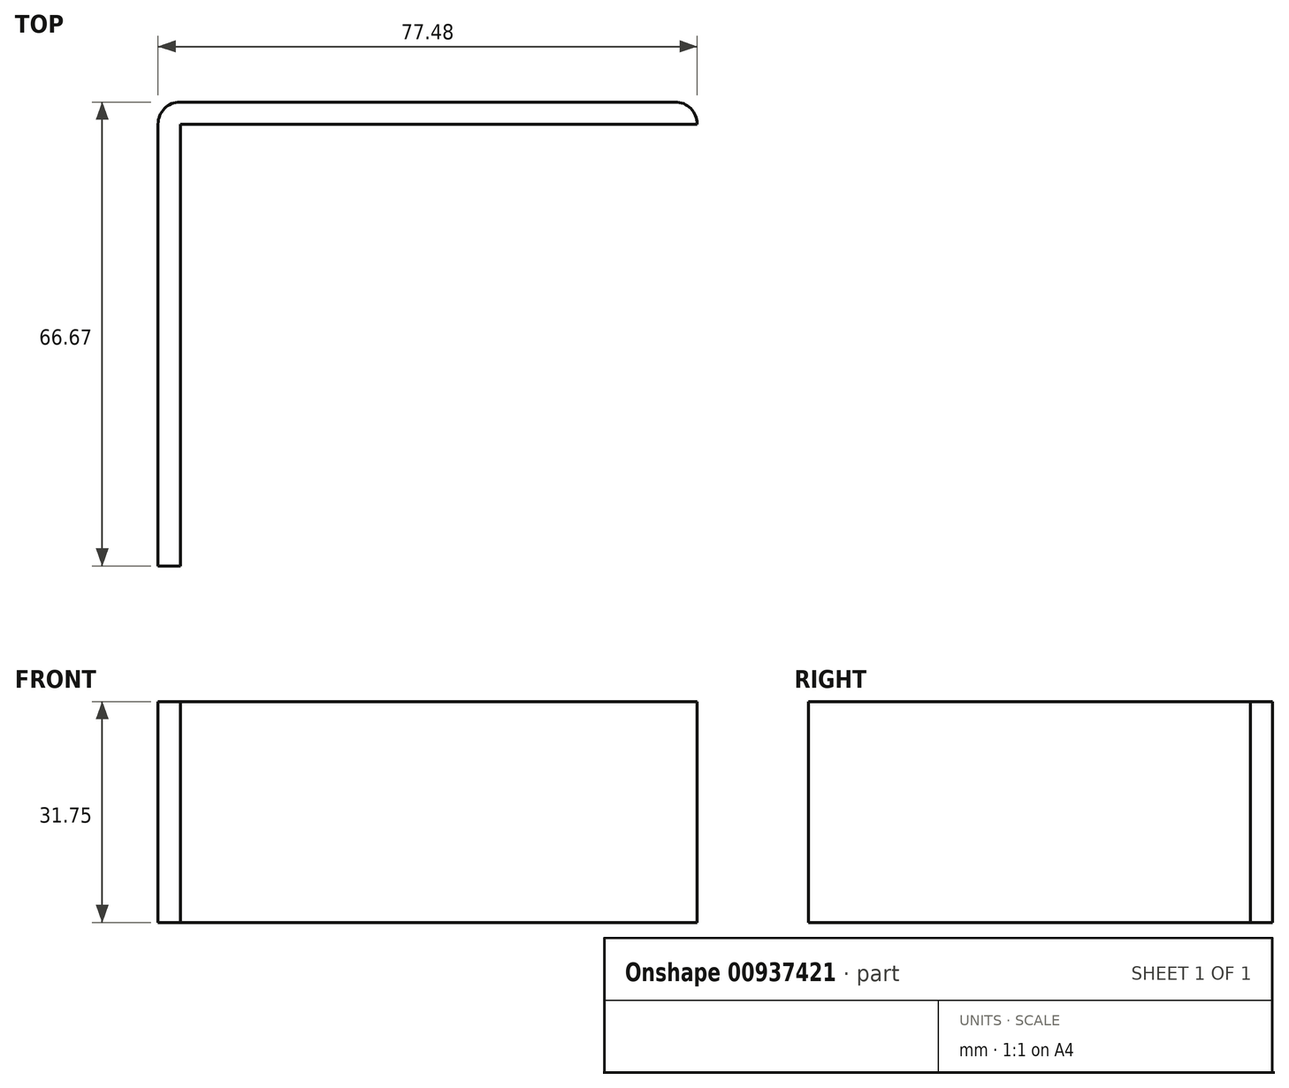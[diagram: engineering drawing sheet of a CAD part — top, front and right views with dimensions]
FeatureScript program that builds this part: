
annotation { "Feature Type Name" : "Feature", "Feature Type Description" : "" }
export const myFeature = defineFeature(function(context is Context, id is Id, definition is map)
    precondition{}
    {
        {
            var Q0;
            Q0=qCreatedBy(makeId("Front.planeOp"),FACE);
            var sketch = newSketch(context, id + "F0", { "sketchPlane" : qUnion([Q0])});
            skLineSegment(sketch, "E0.bottom", {"start": v(0, 0) * mm, "end": v(45.72, 0) * mm});
            skLineSegment(sketch, "E0.top", {"start": v(0, 31.75) * mm, "end": v(45.72, 31.75) * mm});
            skLineSegment(sketch, "E0.left", {"start": v(0, 0) * mm, "end": v(0, 31.75) * mm});
            skLineSegment(sketch, "E0.right", {"start": v(45.72, 0) * mm, "end": v(45.72, 31.75) * mm});
            skSolve(sketch);
        }
        {
            var Q0;
            Q0=makeQuery(id+"F0.imprint","IMPRINT",FACE,{"disambiguationData":[TD([[makeQuery(id+"F0.imprint","IMPRINT",EDGE,{"derivedFrom":sQuery(id+"F0.wireOp",EDGE,"E0.bottom")}),1.0]])]});
            extrude(context, id + "F1", {"entities" : qUnion([Q0]), "depth" : 3.17 * mm, "offsetDistance" : 25.4 * mm});
        }
        {
            var Q0;
            Q0=makeQuery(id+"F1.opExtrude","SWEPT_FACE",FACE,{"disambiguationData":[OSD([sQuery(id+"F0.wireOp",EDGE,"E0.right")])]});
            var Q1;
            Q1=makeQuery(id+"F1.opExtrude","CAP_EDGE",EDGE,{"disambiguationData":[OSD([sQuery(id+"F0.wireOp",EDGE,"E0.right")])],"isStart":false});
            revolve(context, id + "F2", {"operationType" : NewBodyOperationType.ADD, "surfaceOperationType" : NewSurfaceOperationType.NEW, "entities" : qUnion([Q0]), "axis" : qUnion([Q1]), "revolveType" : RevolveType.ONE_DIRECTION, "oppositeDirection" : true, "angle" : 90 * degree});
        }
        {
            var Q0;
            Q0=makeQuery(id+"F1.opExtrude","SWEPT_FACE",FACE,{"disambiguationData":[OSD([sQuery(id+"F0.wireOp",EDGE,"E0.left")])]});
            extrude(context, id + "F3", {"entities" : qUnion([Q0]), "operationType" : NewBodyOperationType.ADD, "depth" : 25.4 * mm, "offsetDistance" : 25.4 * mm});
        }
        {
            var Q0;
            Q0=makeQuery(id+"F3.opExtrude","CAP_FACE",FACE,{"disambiguationData":[OSD([sQuery(id+"F0.wireOp",EDGE,"E0.left")])],"isStart":false});
            var Q1;
            {var subQ0=sQuery(id+"F0.wireOp",EDGE,"E0.left");Q1=makeQuery(id+"F3.opExtrude","CAP_EDGE",EDGE,{"disambiguationData":[OSD([subQ0]),TDD([makeQuery(id+"F1.opExtrude","CAP_EDGE",EDGE,{"disambiguationData":[OSD([subQ0])],"isStart":false})])],"isStart":false});}
            revolve(context, id + "F4", {"operationType" : NewBodyOperationType.ADD, "surfaceOperationType" : NewSurfaceOperationType.NEW, "entities" : qUnion([Q0]), "axis" : qUnion([Q1]), "revolveType" : RevolveType.SYMMETRIC, "angle" : 180 * degree});
        }
        {
            var Q0;
            {var subQ0=sQuery(id+"F0.wireOp",EDGE,"E0.left");var subQ1=sQuery(id+"F0.wireOp",EDGE,"E0.right");Q0=makeQuery(id+"F4.boolean.opBoolean","MERGE",FACE,{"derivedFrom":[makeQuery(id+"F3.boolean.opBoolean","MERGE",FACE,{"derivedFrom":[makeQuery(id+"F2.boolean.opBoolean","MERGE",FACE,{"derivedFrom":[makeQuery(id+"F1.opExtrude","CAP_FACE",FACE,{"disambiguationData":[OSD([sQuery(id+"F0.wireOp",EDGE,"E0.bottom"),sQuery(id+"F0.wireOp",EDGE,"E0.top"),subQ0,subQ1])],"isStart":false}),makeQuery(id+"F2.opRevolve","CAP_FACE",FACE,{"disambiguationData":[OSD([subQ1])],"isStart":false})]}),makeQuery(id+"F3.opExtrude","SWEPT_FACE",FACE,{"disambiguationData":[OSD([subQ0]),TDD([makeQuery(id+"F1.opExtrude","CAP_EDGE",EDGE,{"disambiguationData":[OSD([subQ0])],"isStart":false})])]})]}),makeQuery(id+"F4.opRevolve","CAP_FACE",FACE,{"disambiguationData":[OSD([subQ0])],"isStart":false})]});}
            var sketch = newSketch(context, id + "F5", { "sketchPlane" : qUnion([Q0])});
            skLineSegment(sketch, "E1.bottom", {"start": v(-28.57, 0) * mm, "end": v(-25.38, 0) * mm});
            skLineSegment(sketch, "E1.top", {"start": v(-28.57, 31.75) * mm, "end": v(-25.38, 31.75) * mm});
            skLineSegment(sketch, "E1.left", {"start": v(-28.57, 0) * mm, "end": v(-28.57, 31.75) * mm});
            skLineSegment(sketch, "E1.right", {"start": v(-25.38, 0) * mm, "end": v(-25.38, 31.75) * mm});
            skSolve(sketch);
        }
        {
            var Q0;
            Q0=makeQuery(id+"F5.imprint","IMPRINT",FACE,{"disambiguationData":[TD([[makeQuery(id+"F5.imprint","IMPRINT",EDGE,{"derivedFrom":sQuery(id+"F5.wireOp",EDGE,"E1.bottom")}),1.0]])]});
            extrude(context, id + "F6", {"entities" : qUnion([Q0]), "operationType" : NewBodyOperationType.ADD, "depth" : 63.5 * mm, "offsetDistance" : 25.4 * mm});
        }
    });
